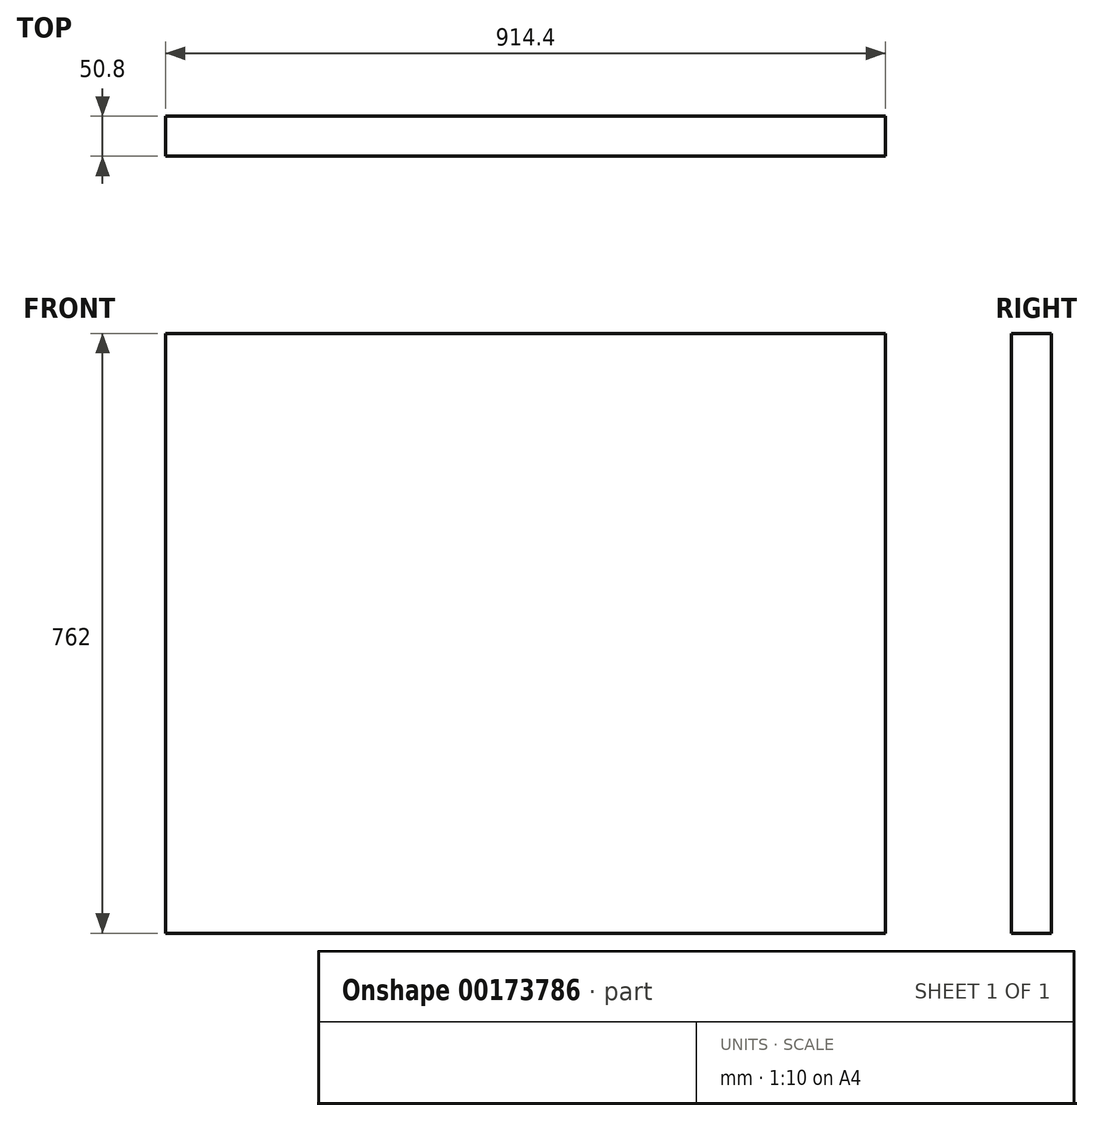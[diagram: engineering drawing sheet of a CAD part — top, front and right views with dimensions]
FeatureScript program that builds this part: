
annotation { "Feature Type Name" : "Feature", "Feature Type Description" : "" }
export const myFeature = defineFeature(function(context is Context, id is Id, definition is map)
    precondition{}
    {
        {
            var Q0;
            Q0=qCreatedBy(makeId("Front.planeOp"),FACE);
            var sketch = newSketch(context, id + "F0", { "sketchPlane" : qUnion([Q0])});
            skLineSegment(sketch, "E0.bottom", {"start": v(457.2, 381) * mm, "end": v(-457.2, 381) * mm});
            skLineSegment(sketch, "E0.top", {"start": v(457.2, -381) * mm, "end": v(-457.2, -381) * mm});
            skLineSegment(sketch, "E0.left", {"start": v(457.2, 381) * mm, "end": v(457.2, -381) * mm});
            skLineSegment(sketch, "E0.right", {"start": v(-457.2, 381) * mm, "end": v(-457.2, -381) * mm});
            skPoint(sketch, "E0.middle", {"position": v(0, 0) * mm});
            skSolve(sketch);
        }
        {
            var Q0;
            Q0 = qSketchRegion(id + "F0", true);
            extrude(context, id + "F1", {"entities" : qUnion([Q0]), "depth" : 50.8 * mm});
        }
    });
